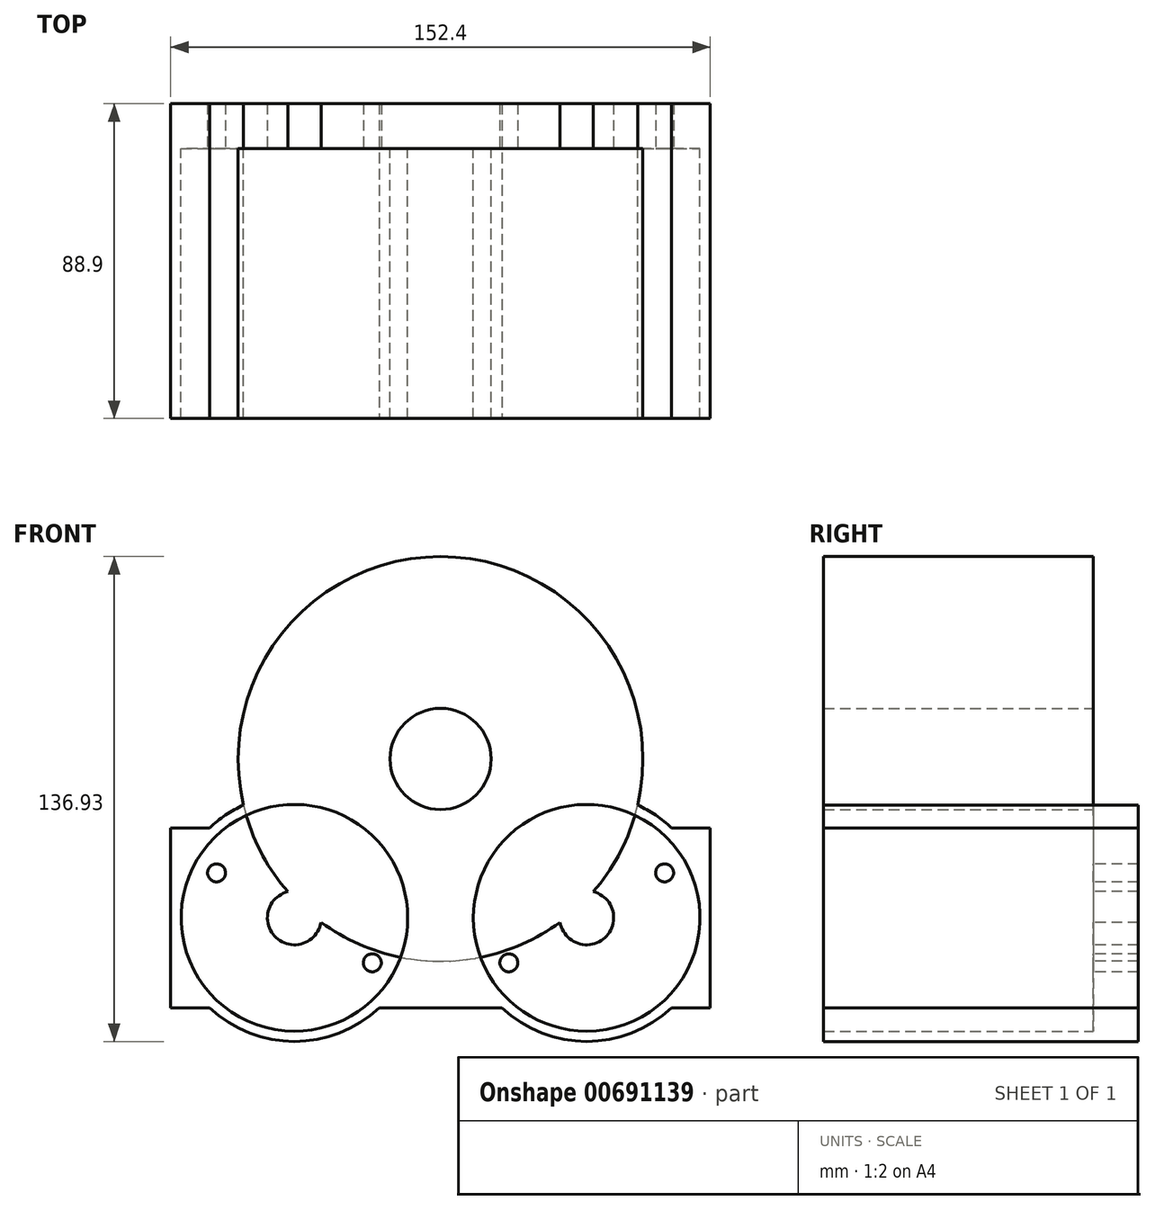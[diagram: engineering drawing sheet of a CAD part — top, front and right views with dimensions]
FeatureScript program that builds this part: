
annotation { "Feature Type Name" : "Feature", "Feature Type Description" : "" }
export const myFeature = defineFeature(function(context is Context, id is Id, definition is map)
    precondition{}
    {
        {
            var Q0;
            Q0=qCreatedBy(makeId("Front.planeOp"),FACE);
            var sketch = newSketch(context, id + "F0", { "sketchPlane" : qUnion([Q0])});
            skLineSegment(sketch, "E0.bottom", {"start": v(0, 0) * mm, "end": v(76.2, 0) * mm, "construction": true});
            skLineSegment(sketch, "E0.top", {"start": v(0, 50.8) * mm, "end": v(76.2, 50.8) * mm, "construction": true});
            skLineSegment(sketch, "E0.left", {"start": v(0, 0) * mm, "end": v(0, 50.8) * mm});
            skLineSegment(sketch, "E0.right", {"start": v(76.2, 0) * mm, "end": v(76.2, 50.8) * mm});
            skLineSegment(sketch, "E1", {"start": v(0, 25.4) * mm, "end": v(76.2, 25.4) * mm, "construction": true});
            skCircle(sketch, "E2", {"center": v(34.93, 25.4) * mm, "radius": 34.93 * mm, "construction": true});
            skLineSegment(sketch, "E3", {"start": v(76.2, 25.4) * mm, "end": v(76.2, 70.26) * mm, "construction": true});
            skLineSegment(sketch, "E4", {"start": v(34.92, 25.4) * mm, "end": v(76.2, 70.26) * mm, "construction": true});
            skCircle(sketch, "E5", {"center": v(34.93, 25.4) * mm, "radius": 7.62 * mm, "construction": true});
            skCircle(sketch, "E6", {"center": v(76.2, 70.26) * mm, "radius": 53.34 * mm, "construction": true});
            skArc(sketch, "E7", {"start": v(10.95, 0) * mm, "mid": v(34.92, -9.53) * mm, "end": v(58.9, 0) * mm});
            skLineSegment(sketch, "E8", {"start": v(0, 50.8) * mm, "end": v(10.95, 50.8) * mm});
            skArc(sketch, "E9", {"start": v(10.95, 50.8) * mm, "mid": v(34.92, 60.33) * mm, "end": v(58.9, 50.8) * mm});
            skLineSegment(sketch, "E10", {"start": v(58.9, 50.8) * mm, "end": v(76.2, 50.8) * mm});
            skLineSegment(sketch, "E11.MirrorCS", {"start": v(152.4, 0) * mm, "end": v(152.4, 50.8) * mm});
            skArc(sketch, "E12.MirrorCS", {"start": v(141.45, 50.8) * mm, "mid": v(117.48, 60.33) * mm, "end": v(93.5, 50.8) * mm});
            skLineSegment(sketch, "E13.MirrorCS", {"start": v(152.4, 50.8) * mm, "end": v(141.45, 50.8) * mm});
            skLineSegment(sketch, "E14.MirrorCS", {"start": v(93.5, 50.8) * mm, "end": v(76.2, 50.8) * mm});
            skArc(sketch, "E15.MirrorCS", {"start": v(141.45, 0) * mm, "mid": v(117.48, -9.52) * mm, "end": v(93.5, 0) * mm});
            skLineSegment(sketch, "E16", {"start": v(10.95, 0) * mm, "end": v(0, 0) * mm});
            skLineSegment(sketch, "E17.MirrorCS", {"start": v(141.45, 0) * mm, "end": v(152.4, 0) * mm});
            skLineSegment(sketch, "E18", {"start": v(58.9, 0) * mm, "end": v(76.2, 0) * mm});
            skLineSegment(sketch, "E19.MirrorCS", {"start": v(93.5, 0) * mm, "end": v(76.2, 0) * mm});
            skLineSegment(sketch, "E20", {"start": v(0, 38.1) * mm, "end": v(76.2, 38.1) * mm, "construction": true});
            skCircle(sketch, "E21", {"center": v(12.93, 38.1) * mm, "radius": 2.54 * mm});
            skCircle(sketch, "E22", {"center": v(34.93, 25.4) * mm, "radius": 25.4 * mm, "construction": true});
            skLineSegment(sketch, "E23", {"start": v(12.93, 38.1) * mm, "end": v(34.93, 25.4) * mm, "construction": true});
            skLineSegment(sketch, "E24", {"start": v(34.93, 25.4) * mm, "end": v(22.23, 3.4) * mm, "construction": true});
            skCircle(sketch, "E25.MirrorC", {"center": v(56.92, 12.7) * mm, "radius": 2.54 * mm});
            skCircle(sketch, "E26.MirrorC", {"center": v(139.47, 38.1) * mm, "radius": 2.54 * mm});
            skCircle(sketch, "E27.MirrorC", {"center": v(95.48, 12.7) * mm, "radius": 2.54 * mm});
            skCircle(sketch, "E28", {"center": v(34.93, 25.4) * mm, "radius": 9.53 * mm, "construction": true});
            skArc(sketch, "E29", {"start": v(40.8, 25.4) * mm, "mid": v(75.16, 13.12) * mm, "end": v(109.96, 24.15) * mm, "construction": true});
            skArc(sketch, "E30", {"start": v(20.56, 57.23) * mm, "mid": v(25.31, 44.25) * mm, "end": v(33.05, 32.79) * mm});
            skArc(sketch, "E31", {"start": v(33.05, 32.79) * mm, "mid": v(29.77, 19.8) * mm, "end": v(42.44, 24.15) * mm});
            skArc(sketch, "E32.trimOffspring", {"start": v(40.8, 25.4) * mm, "mid": v(75.16, 13.12) * mm, "end": v(109.96, 24.15) * mm});
            skArc(sketch, "E33.MirrorCS", {"start": v(119.35, 32.79) * mm, "mid": v(122.63, 19.8) * mm, "end": v(109.96, 24.15) * mm});
            skCircle(sketch, "E34.MirrorC", {"center": v(117.48, 25.4) * mm, "radius": 7.62 * mm, "construction": true});
            skArc(sketch, "E35.trimOffspring", {"start": v(119.35, 32.79) * mm, "mid": v(76.2, 127.41) * mm, "end": v(33.05, 32.79) * mm, "construction": true});
            skArc(sketch, "E36.trimOffspring", {"start": v(119.35, 32.79) * mm, "mid": v(127.09, 44.25) * mm, "end": v(131.84, 57.23) * mm});
            skCircle(sketch, "E37", {"center": v(34.93, 25.4) * mm, "radius": 32 * mm, "construction": true});
            skSolve(sketch);
        }
        {
            var Q0;
            Q0=makeQuery(id+"F0.imprint","IMPRINT",FACE,{"disambiguationData":[TD([[makeQuery(id+"F0.imprint","IMPRINT",EDGE,{"derivedFrom":sQuery(id+"F0.wireOp",EDGE,"E0.left")}),-1.0]])]});
            var Q1;
            Q1=makeQuery(id+"F0.imprint","IMPRINT",FACE,{"disambiguationData":[TD([[makeQuery(id+"F0.imprint","IMPRINT",EDGE,{"derivedFrom":sQuery(id+"F0.wireOp",EDGE,"E11.MirrorCS")}),1.0]])]});
            extrude(context, id + "F1", {"entities" : qUnion([Q0, Q1]), "oppositeDirection" : true, "depth" : 12.7 * mm, "offsetDistance" : 25.4 * mm});
        }
        {
            var Q0;
            Q0=makeQuery(id+"F1.opExtrude","CAP_FACE",FACE,{"disambiguationData":[OSD([sQuery(id+"F0.wireOp",EDGE,"E0.left"),sQuery(id+"F0.wireOp",EDGE,"E7"),sQuery(id+"F0.wireOp",EDGE,"E8"),sQuery(id+"F0.wireOp",EDGE,"E9"),sQuery(id+"F0.wireOp",EDGE,"E11.MirrorCS"),sQuery(id+"F0.wireOp",EDGE,"E12.MirrorCS"),sQuery(id+"F0.wireOp",EDGE,"E13.MirrorCS"),sQuery(id+"F0.wireOp",EDGE,"E15.MirrorCS"),sQuery(id+"F0.wireOp",EDGE,"E16"),sQuery(id+"F0.wireOp",EDGE,"E17.MirrorCS"),sQuery(id+"F0.wireOp",EDGE,"E18"),sQuery(id+"F0.wireOp",EDGE,"E19.MirrorCS"),sQuery(id+"F0.wireOp",EDGE,"E21"),sQuery(id+"F0.wireOp",EDGE,"E25.MirrorC"),sQuery(id+"F0.wireOp",EDGE,"E26.MirrorC"),sQuery(id+"F0.wireOp",EDGE,"E27.MirrorC"),sQuery(id+"F0.wireOp",EDGE,"E30"),sQuery(id+"F0.wireOp",EDGE,"E31"),sQuery(id+"F0.wireOp",EDGE,"E32.trimOffspring"),sQuery(id+"F0.wireOp",EDGE,"E33.MirrorCS"),sQuery(id+"F0.wireOp",EDGE,"E36.trimOffspring")])],"isStart":true});
            var sketch = newSketch(context, id + "F2", { "sketchPlane" : qUnion([Q0])});
            skArc(sketch, "E38", {"start": v(64.92, 14.24) * mm, "mid": v(76.2, 13.11) * mm, "end": v(87.48, 14.24) * mm, "construction": true});
            skCircle(sketch, "E39", {"center": v(34.93, 25.4) * mm, "radius": 32 * mm, "construction": true});
            skArc(sketch, "E40", {"start": v(64.92, 14.24) * mm, "mid": v(13.26, 1.85) * mm, "end": v(21.3, 54.36) * mm});
            skArc(sketch, "E41", {"start": v(76.2, 13.11) * mm, "mid": v(70.53, 13.4) * mm, "end": v(64.92, 14.24) * mm});
            skLineSegment(sketch, "E42", {"start": v(76.2, 13.11) * mm, "end": v(76.2, 70.26) * mm, "construction": true});
            skArc(sketch, "E43.MirrorCS", {"start": v(87.48, 14.24) * mm, "mid": v(139.14, 1.85) * mm, "end": v(131.1, 54.36) * mm});
            skCircle(sketch, "E44.MirrorC", {"center": v(117.48, 25.4) * mm, "radius": 32 * mm, "construction": true});
            skArc(sketch, "E45.MirrorC", {"start": v(20.56, 57.23) * mm, "mid": v(76.2, 127.41) * mm, "end": v(131.84, 57.23) * mm, "construction": true});
            skArc(sketch, "E46", {"start": v(20.56, 57.23) * mm, "mid": v(15.49, 54.42) * mm, "end": v(10.95, 50.8) * mm});
            skArc(sketch, "E47.MirrorCS", {"start": v(131.84, 57.23) * mm, "mid": v(136.91, 54.42) * mm, "end": v(141.45, 50.8) * mm});
            skArc(sketch, "E48", {"start": v(58.9, 0) * mm, "mid": v(34.92, -9.53) * mm, "end": v(10.95, 0) * mm});
            skLineSegment(sketch, "E49", {"start": v(10.95, 0) * mm, "end": v(0, 0) * mm});
            skLineSegment(sketch, "E50", {"start": v(0, 0) * mm, "end": v(0, 50.8) * mm});
            skLineSegment(sketch, "E51", {"start": v(0, 50.8) * mm, "end": v(10.95, 50.8) * mm});
            skLineSegment(sketch, "E52", {"start": v(76.2, 0) * mm, "end": v(58.9, 0) * mm});
            skArc(sketch, "E53.MirrorCS", {"start": v(93.5, 0) * mm, "mid": v(117.48, -9.52) * mm, "end": v(141.45, 0) * mm});
            skLineSegment(sketch, "E54.MirrorCS", {"start": v(76.2, 0) * mm, "end": v(93.5, 0) * mm});
            skLineSegment(sketch, "E55.MirrorCS", {"start": v(152.4, 0) * mm, "end": v(152.4, 50.8) * mm});
            skLineSegment(sketch, "E56.MirrorCS", {"start": v(141.45, 0) * mm, "end": v(152.4, 0) * mm});
            skLineSegment(sketch, "E57.MirrorCS", {"start": v(152.4, 50.8) * mm, "end": v(141.45, 50.8) * mm});
            skPoint(sketch, "E58.end.orphan", {"position": v(76.2, 127.41) * mm});
            skArc(sketch, "E59.trimOffspring", {"start": v(131.84, 57.23) * mm, "mid": v(76.2, 127.41) * mm, "end": v(20.56, 57.23) * mm, "construction": true});
            skArc(sketch, "E60.trimOffspring", {"start": v(87.48, 14.24) * mm, "mid": v(76.2, 13.11) * mm, "end": v(64.92, 14.24) * mm, "construction": true});
            skArc(sketch, "E61", {"start": v(20.56, 57.23) * mm, "mid": v(76.2, 127.41) * mm, "end": v(131.84, 57.23) * mm});
            skCircle(sketch, "E62", {"center": v(34.93, 25.4) * mm, "radius": 32 * mm});
            skCircle(sketch, "E63.MirrorC", {"center": v(117.48, 25.4) * mm, "radius": 32 * mm});
            skPoint(sketch, "E64.center.orphan", {"position": v(12.93, 38.1) * mm});
            skPoint(sketch, "E65.center.orphan", {"position": v(56.92, 12.7) * mm});
            skCircle(sketch, "E66", {"center": v(76.2, 70.26) * mm, "radius": 14.29 * mm});
            skSolve(sketch);
        }
        {
            var Q0;
            {var subQ5=sQuery(id+"F2.wireOp",EDGE,"E41");Q0=makeQuery(id+"F2.imprint","IMPRINT",FACE,{"disambiguationData":[TD([[makeQuery(id+"F2.imprint","IMPRINT",EDGE,{"derivedFrom":subQ5}),-1.0]])]});}
            var Q1;
            {var subQ5=sQuery(id+"F2.wireOp",EDGE,"E41");Q1=makeQuery(id+"F2.imprint","IMPRINT",FACE,{"disambiguationData":[TD([[makeQuery(id+"F2.imprint","IMPRINT",EDGE,{"derivedFrom":subQ5}),1.0]])]});}
            extrude(context, id + "F3", {"entities" : qUnion([Q0, Q1]), "operationType" : NewBodyOperationType.ADD, "depth" : 76.2 * mm, "offsetDistance" : 25.4 * mm});
        }
    });
